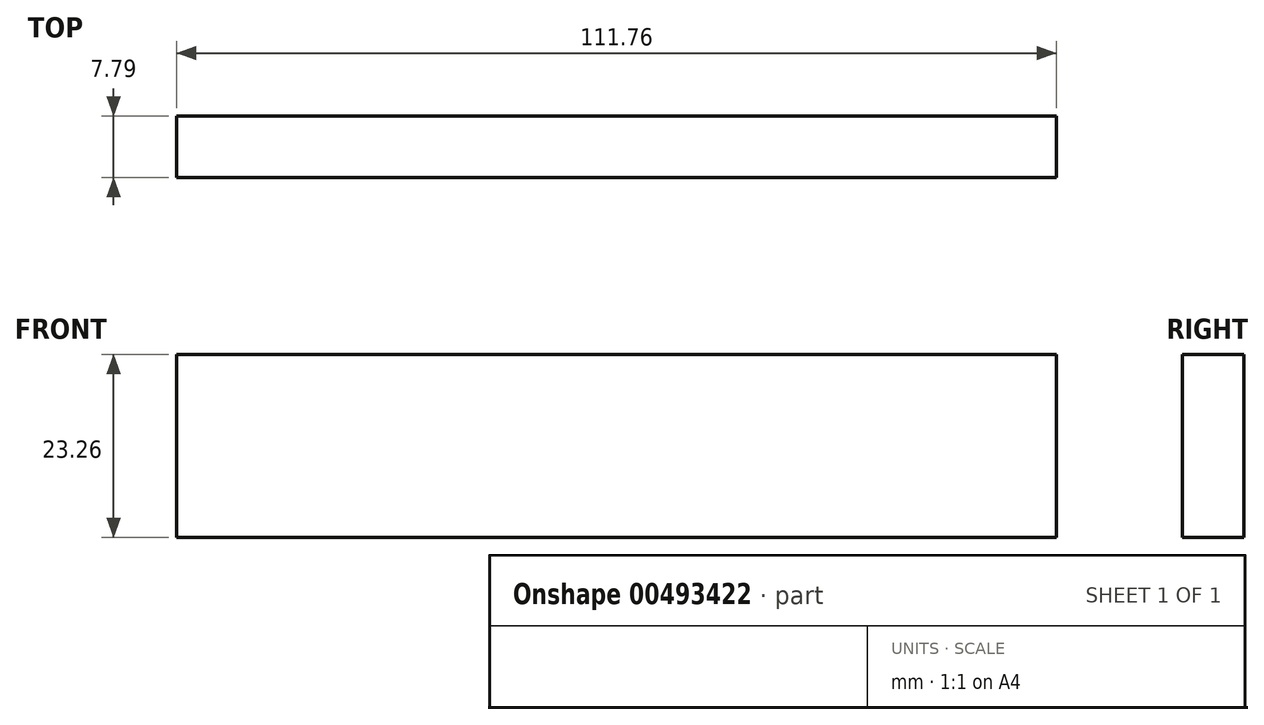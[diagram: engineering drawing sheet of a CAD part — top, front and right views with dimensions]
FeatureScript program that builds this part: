
annotation { "Feature Type Name" : "Feature", "Feature Type Description" : "" }
export const myFeature = defineFeature(function(context is Context, id is Id, definition is map)
    precondition{}
    {
        {
            var Q0;
            Q0=qCreatedBy(makeId("Front.planeOp"),FACE);
            var sketch = newSketch(context, id + "F0", { "sketchPlane" : qUnion([Q0])});
            skLineSegment(sketch, "E0.bottom", {"start": v(44.51, 17.24) * mm, "end": v(-67.25, 17.24) * mm});
            skLineSegment(sketch, "E0.top", {"start": v(44.51, -6.02) * mm, "end": v(-67.25, -6.02) * mm});
            skLineSegment(sketch, "E0.left", {"start": v(44.51, 17.24) * mm, "end": v(44.51, -6.02) * mm});
            skLineSegment(sketch, "E0.right", {"start": v(-67.25, 17.24) * mm, "end": v(-67.25, -6.02) * mm});
            skPoint(sketch, "E0.middle", {"position": v(-11.37, 5.6) * mm});
            skSolve(sketch);
        }
        {
            var Q0;
            Q0=makeQuery(id+"F0.imprint","IMPRINT",FACE,{"disambiguationData":[TD([[makeQuery(id+"F0.imprint","IMPRINT",EDGE,{"derivedFrom":sQuery(id+"F0.wireOp",EDGE,"E0.bottom")}),1.0]])]});
            extrude(context, id + "F1", {"entities" : qUnion([Q0]), "depth" : 7.8 * mm});
        }
    });
